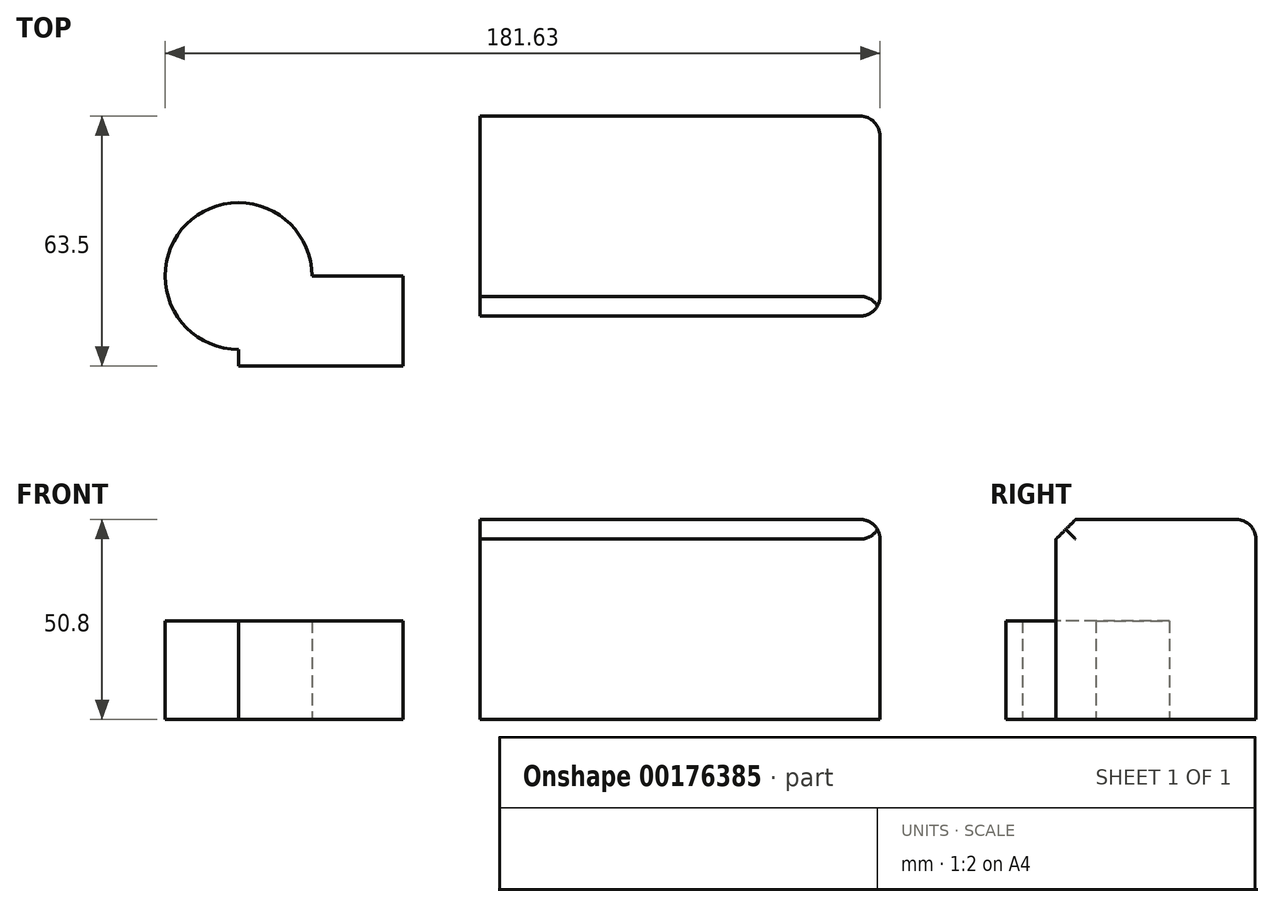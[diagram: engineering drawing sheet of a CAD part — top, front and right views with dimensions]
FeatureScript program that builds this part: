
annotation { "Feature Type Name" : "Feature", "Feature Type Description" : "" }
export const myFeature = defineFeature(function(context is Context, id is Id, definition is map)
    precondition{}
    {
        {
            var Q0;
            Q0=qCreatedBy(makeId("Top.planeOp"),FACE);
            var sketch = newSketch(context, id + "F0", { "sketchPlane" : qUnion([Q0])});
            skLineSegment(sketch, "E0.bottom", {"start": v(0, 0) * mm, "end": v(101.6, 0) * mm});
            skLineSegment(sketch, "E0.top", {"start": v(0, -50.8) * mm, "end": v(101.6, -50.8) * mm});
            skLineSegment(sketch, "E0.left", {"start": v(0, 0) * mm, "end": v(0, -50.8) * mm});
            skLineSegment(sketch, "E0.right", {"start": v(101.6, 0) * mm, "end": v(101.6, -50.8) * mm});
            skSolve(sketch);
        }
        {
            var Q0;
            Q0=makeQuery(id+"F0.imprint","IMPRINT",FACE,{"disambiguationData":[TD([[makeQuery(id+"F0.imprint","IMPRINT",EDGE,{"derivedFrom":sQuery(id+"F0.wireOp",EDGE,"E0.bottom")}),-1.0]])]});
            var Q1;
            Q1 = qSketchRegion(id + "F0", true);
            extrude(context, id + "F1", {"entities" : qUnion([Q0, Q1]), "depth" : 50.8 * mm});
        }
        {
            var Q0;
            Q0=makeQuery(id+"F1.opExtrude","SWEPT_EDGE",EDGE,{"disambiguationData":[OSD([sQuery(id+"F0.wireOp",EDGE,"E0.bottom"),sQuery(id+"F0.wireOp",EDGE,"E0.right")])]});
            fillet(context, id + "F2", {"entities" : qUnion([Q0]), "radius" : 5.08 * mm, "tangentPropagation" : true, "allowEdgeOverflow" : false});
        }
        {
            var Q0;
            Q0=qCreatedBy(makeId("Top.planeOp"),FACE);
            var sketch = newSketch(context, id + "F3", { "sketchPlane" : qUnion([Q0])});
            skLineSegment(sketch, "E1.bottom", {"start": v(-61.39, -40.62) * mm, "end": v(-19.58, -40.62) * mm});
            skLineSegment(sketch, "E1.top", {"start": v(-61.39, -63.5) * mm, "end": v(-19.58, -63.5) * mm});
            skLineSegment(sketch, "E1.left", {"start": v(-61.39, -40.62) * mm, "end": v(-61.39, -63.5) * mm});
            skLineSegment(sketch, "E1.right", {"start": v(-19.58, -40.62) * mm, "end": v(-19.58, -63.5) * mm});
            skCircle(sketch, "E2", {"center": v(-61.39, -40.62) * mm, "radius": 18.64 * mm});
            skSolve(sketch);
        }
        {
            var Q0;
            Q0 = qSketchRegion(id + "F3", true);
            var Q1;
            {var subQ0=sQuery(id+"F3.wireOp",EDGE,"E1.left");var subQ1=sQuery(id+"F3.wireOp",EDGE,"E1.bottom");var subQ2=makeQuery(id+"F3.imprint","INTERSECT",VERTEX,{"derivedFrom":[subQ1,subQ0]});Q1=makeQuery(id+"F3.imprint","IMPRINT",FACE,{"disambiguationData":[TD([[makeQuery(id+"F3.imprint","IMPRINT",EDGE,{"disambiguationData":[TD([[subQ2,-1.0]])],"derivedFrom":subQ1}),1.0]])]});}
            extrude(context, id + "F4", {"entities" : qUnion([Q0, Q1]), "depth" : 25 * mm});
        }
        {
            var Q0;
            Q0=makeQuery(id+"F1.opExtrude","CAP_EDGE",EDGE,{"disambiguationData":[OSD([sQuery(id+"F0.wireOp",EDGE,"E0.top")])],"isStart":false});
            chamfer(context, id + "F5", {"entities" : qUnion([Q0]), "width" : 5 * mm, "tangentPropagation" : true});
        }
        {
            var Q0;
            Q0=makeQuery(id+"F1.opExtrude","CAP_EDGE",EDGE,{"disambiguationData":[OSD([sQuery(id+"F0.wireOp",EDGE,"E0.bottom")])],"isStart":false});
            fillet(context, id + "F6", {"entities" : qUnion([Q0]), "radius" : 5 * mm, "tangentPropagation" : true, "allowEdgeOverflow" : false});
        }
        {
            var Q0;
            Q0=makeQuery(id+"F1.opExtrude","SWEPT_EDGE",EDGE,{"disambiguationData":[OSD([sQuery(id+"F0.wireOp",EDGE,"E0.top"),sQuery(id+"F0.wireOp",EDGE,"E0.right")])]});
            fillet(context, id + "F7", {"entities" : qUnion([Q0]), "radius" : 5 * mm, "tangentPropagation" : true, "allowEdgeOverflow" : false});
        }
    });
